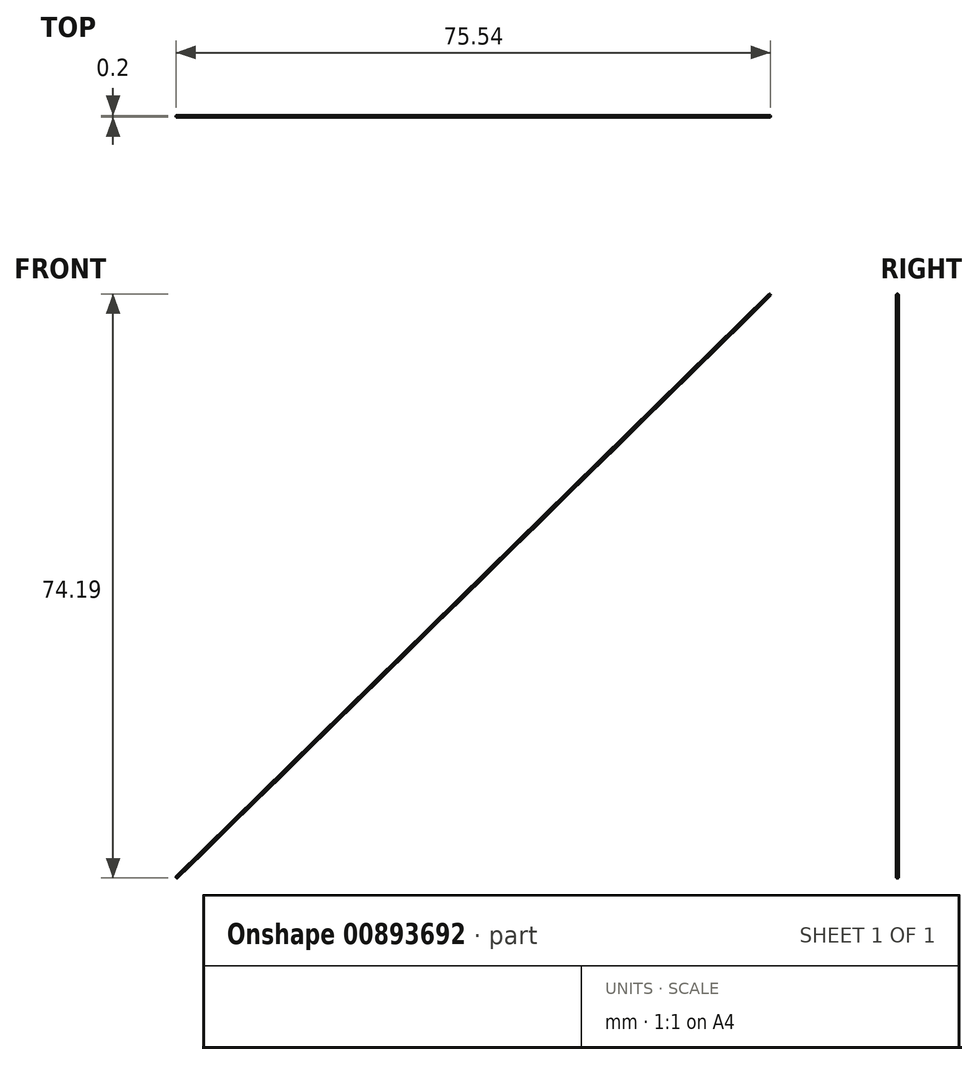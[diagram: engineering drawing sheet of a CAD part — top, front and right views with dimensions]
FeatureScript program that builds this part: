
annotation { "Feature Type Name" : "Feature", "Feature Type Description" : "" }
export const myFeature = defineFeature(function(context is Context, id is Id, definition is map)
    precondition{}
    {
        {
            var Q0;
            Q0=qCreatedBy(makeId("Front.planeOp"),FACE);
            var sketch = newSketch(context, id + "F0", { "sketchPlane" : qUnion([Q0])});
            skLineSegment(sketch, "E0", {"start": v(0, 0) * mm, "end": v(75.4, 74.05) * mm});
            skSolve(sketch);
        }
        {
            var Q0;
            Q0=sQuery(id+"F0.wireOp",EDGE,"E0");
            var Q1;
            Q1=sQuery(id+"F0.wireOp",VERTEX,"E0.end");
            cPlane(context, id + "F1", {"entities" : qUnion([Q0, Q1]), "cplaneType" : CPlaneType.LINE_POINT, "offset" : 25 * mm, "width" : 150 * mm, "height" : 150 * mm});
        }
        {
            var Q0;
            Q0=qCreatedBy(id+"F1.planeOp",FACE);
            var sketch = newSketch(context, id + "F2", { "sketchPlane" : qUnion([Q0])});
            skCircle(sketch, "E1", {"center": v(0, 0) * mm, "radius": 0.1 * mm});
            skSolve(sketch);
        }
        {
            var Q0;
            Q0=makeQuery(id+"F2.imprint","IMPRINT",FACE,{"disambiguationData":[TD([[makeQuery(id+"F2.imprint","IMPRINT",EDGE,{"derivedFrom":sQuery(id+"F2.wireOp",EDGE,"E1")}),1.0]])]});
            var Q1;
            Q1=sQuery(id+"F0.wireOp",EDGE,"E0");
            sweep(context, id + "F3", {"profiles" : qUnion([Q0]), "path" : qUnion([Q1])});
        }
    });
